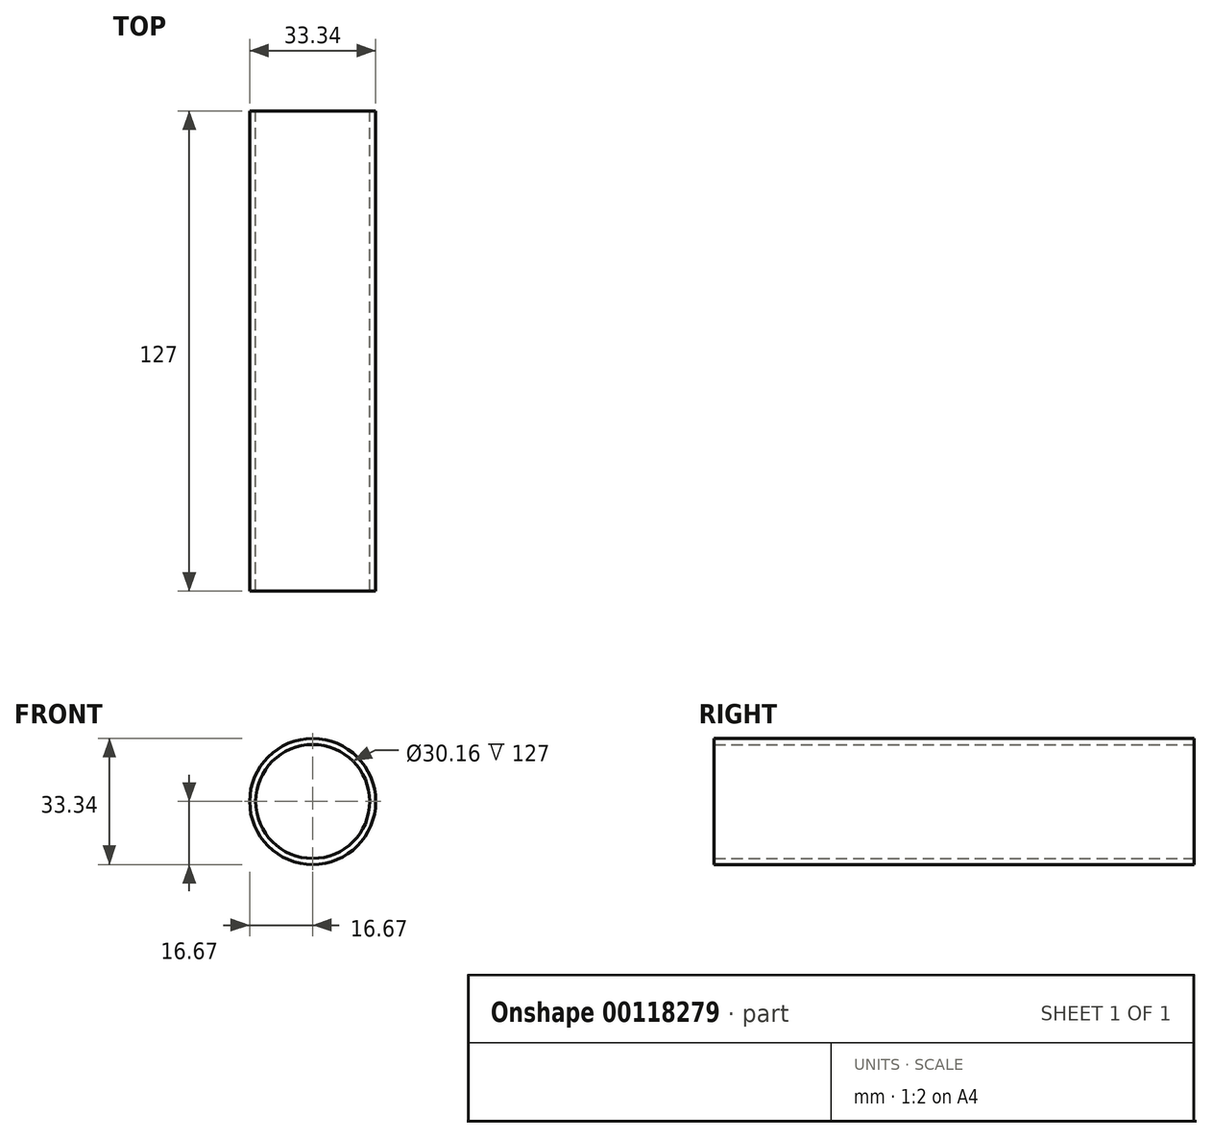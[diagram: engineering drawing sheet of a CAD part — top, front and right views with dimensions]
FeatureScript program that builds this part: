
annotation { "Feature Type Name" : "Feature", "Feature Type Description" : "" }
export const myFeature = defineFeature(function(context is Context, id is Id, definition is map)
    precondition{}
    {
        {
            var Q0;
            Q0=qCreatedBy(makeId("Front.planeOp"),FACE);
            var sketch = newSketch(context, id + "F0", { "sketchPlane" : qUnion([Q0])});
            skCircle(sketch, "E0", {"center": v(0, 0) * mm, "radius": 16.67 * mm});
            skCircle(sketch, "E1", {"center": v(0, 0) * mm, "radius": 15.08 * mm});
            skSolve(sketch);
        }
        {
            var Q0;
            Q0=makeQuery(id+"F0.imprint","IMPRINT",FACE,{"disambiguationData":[TD([[makeQuery(id+"F0.imprint","IMPRINT",EDGE,{"derivedFrom":sQuery(id+"F0.wireOp",EDGE,"E0")}),1.0]])]});
            extrude(context, id + "F1", {"entities" : qUnion([Q0]), "endBound" : BoundingType.SYMMETRIC, "depth" : 127 * mm});
        }
    });
